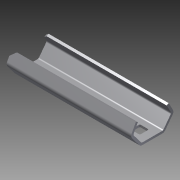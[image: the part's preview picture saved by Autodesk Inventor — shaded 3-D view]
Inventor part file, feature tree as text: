
AUTODESK INVENTOR PART (.ipt)
format: ipt  version: 2014 (Build 180170000, 170)  size: 344,064 bytes
history: native  units: in
note: dims shown in document units (in); Inventor stores cm internally (conversion verified against a paired STEP export)
features: other x1, imported_body x1, extrude x1, sketch x1
ambient origin geometry x8: Origin, YZ Plane, XZ Plane, XY Plane, X Axis, Y Axis, Z Axis, Center Point
bodies: Body1 (feature_tree)
feature tree (4):
  parser-record x1  (decoder bookkeeping rows leaked as tree rows — omitted from the tree; the rows remain in map.json)
  imported_body  "Base1"
  extrude  "Extrusion1"  Depth=1.0in TaperAngle=0.0deg
  sketch  "Sketch1"  dims[d0=2.5in d1=1.0in d2=0.0in]
